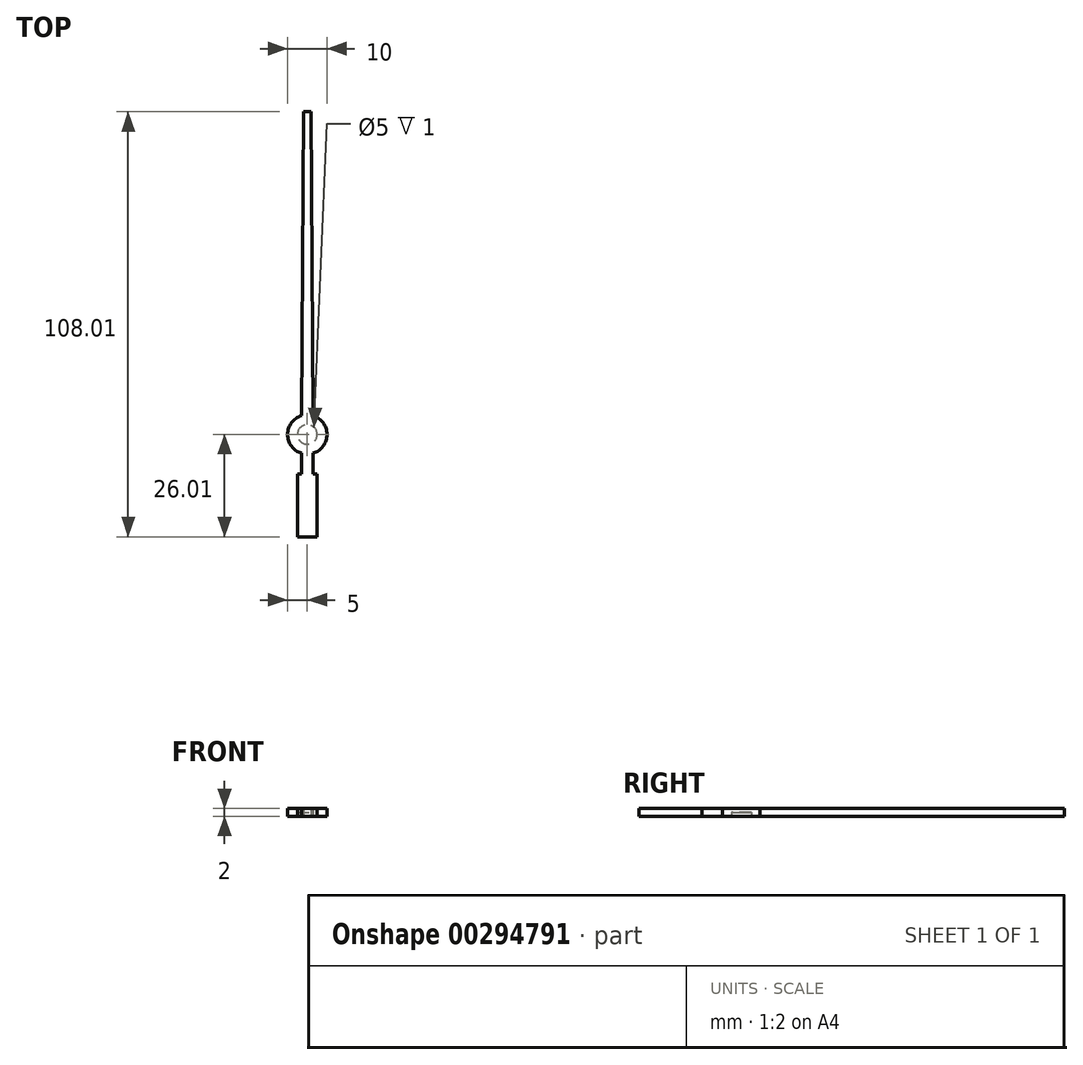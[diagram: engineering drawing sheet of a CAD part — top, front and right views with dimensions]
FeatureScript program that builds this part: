
annotation { "Feature Type Name" : "Feature", "Feature Type Description" : "" }
export const myFeature = defineFeature(function(context is Context, id is Id, definition is map)
    precondition{}
    {
        {
            var Q0;
            Q0=qCreatedBy(makeId("Top.planeOp"),FACE);
            var sketch = newSketch(context, id + "F0", { "sketchPlane" : qUnion([Q0])});
            skCircle(sketch, "E0", {"center": v(0, 0) * mm, "radius": 5 * mm});
            skLineSegment(sketch, "E1", {"start": v(-1.5, 0) * mm, "end": v(1.5, 0) * mm});
            skLineSegment(sketch, "E2", {"start": v(0, 0) * mm, "end": v(0, 82) * mm});
            skLineSegment(sketch, "E3", {"start": v(-1, 82) * mm, "end": v(1, 82) * mm});
            skLineSegment(sketch, "E4", {"start": v(-1, 82) * mm, "end": v(-1.5, 0) * mm});
            skLineSegment(sketch, "E5", {"start": v(1, 82) * mm, "end": v(1.5, 0) * mm});
            skLineSegment(sketch, "E6", {"start": v(-1.5, 0) * mm, "end": v(-1.5, -26) * mm});
            skLineSegment(sketch, "E7", {"start": v(1.5, 0) * mm, "end": v(1.5, -26) * mm});
            skLineSegment(sketch, "E8", {"start": v(-2.5, -9.99) * mm, "end": v(2.5, -9.99) * mm});
            skLineSegment(sketch, "E9", {"start": v(-2.5, -9.99) * mm, "end": v(-2.5, -25.99) * mm});
            skLineSegment(sketch, "E10", {"start": v(2.5, -9.99) * mm, "end": v(2.5, -26.01) * mm});
            skLineSegment(sketch, "E11", {"start": v(2.5, -26.01) * mm, "end": v(-2.5, -25.99) * mm});
            skLineSegment(sketch, "E12", {"start": v(-1.5, -26) * mm, "end": v(1.5, -26) * mm});
            skPoint(sketch, "E13", {"position": v(0, -26) * mm});
            skSolve(sketch);
        }
        {
            var Q0;
            Q0 = qSketchRegion(id + "F0", true);
            extrude(context, id + "F1", {"entities" : qUnion([Q0]), "depth" : 2 * mm});
        }
        {
            var Q0;
            Q0=makeQuery(id+"F1.opExtrude","CAP_FACE",FACE,{"disambiguationData":[OSD([sQuery(id+"F0.wireOp",EDGE,"E0"),sQuery(id+"F0.wireOp",EDGE,"E3"),sQuery(id+"F0.wireOp",EDGE,"E4"),sQuery(id+"F0.wireOp",EDGE,"E5"),sQuery(id+"F0.wireOp",EDGE,"E6"),sQuery(id+"F0.wireOp",EDGE,"E7"),sQuery(id+"F0.wireOp",EDGE,"E8"),sQuery(id+"F0.wireOp",EDGE,"E9"),sQuery(id+"F0.wireOp",EDGE,"E10"),sQuery(id+"F0.wireOp",EDGE,"E11"),sQuery(id+"F0.wireOp",EDGE,"E12")])],"isStart":true});
            var sketch = newSketch(context, id + "F2", { "sketchPlane" : qUnion([Q0])});
            skCircle(sketch, "E14", {"center": v(0, 0) * mm, "radius": 2.5 * mm});
            skSolve(sketch);
        }
        {
            var Q0;
            Q0=makeQuery(id+"F2.imprint","IMPRINT",FACE,{"disambiguationData":[TD([[makeQuery(id+"F2.imprint","IMPRINT",EDGE,{"derivedFrom":sQuery(id+"F2.wireOp",EDGE,"E14")}),1.0]])]});
            var sketch = newSketch(context, id + "F3", { "sketchPlane" : qUnion([Q0])});
            skSolve(sketch);
        }
        {
            var Q0;
            Q0 = qSketchRegion(id + "F3", true);
            var Q1;
            Q1=makeQuery(id+"F2.imprint","IMPRINT",FACE,{"disambiguationData":[TD([[makeQuery(id+"F2.imprint","IMPRINT",EDGE,{"derivedFrom":sQuery(id+"F2.wireOp",EDGE,"E14")}),1.0]])]});
            extrude(context, id + "F4", {"entities" : qUnion([Q0, Q1]), "operationType" : NewBodyOperationType.REMOVE, "oppositeDirection" : true, "depth" : 1 * mm});
        }
    });
